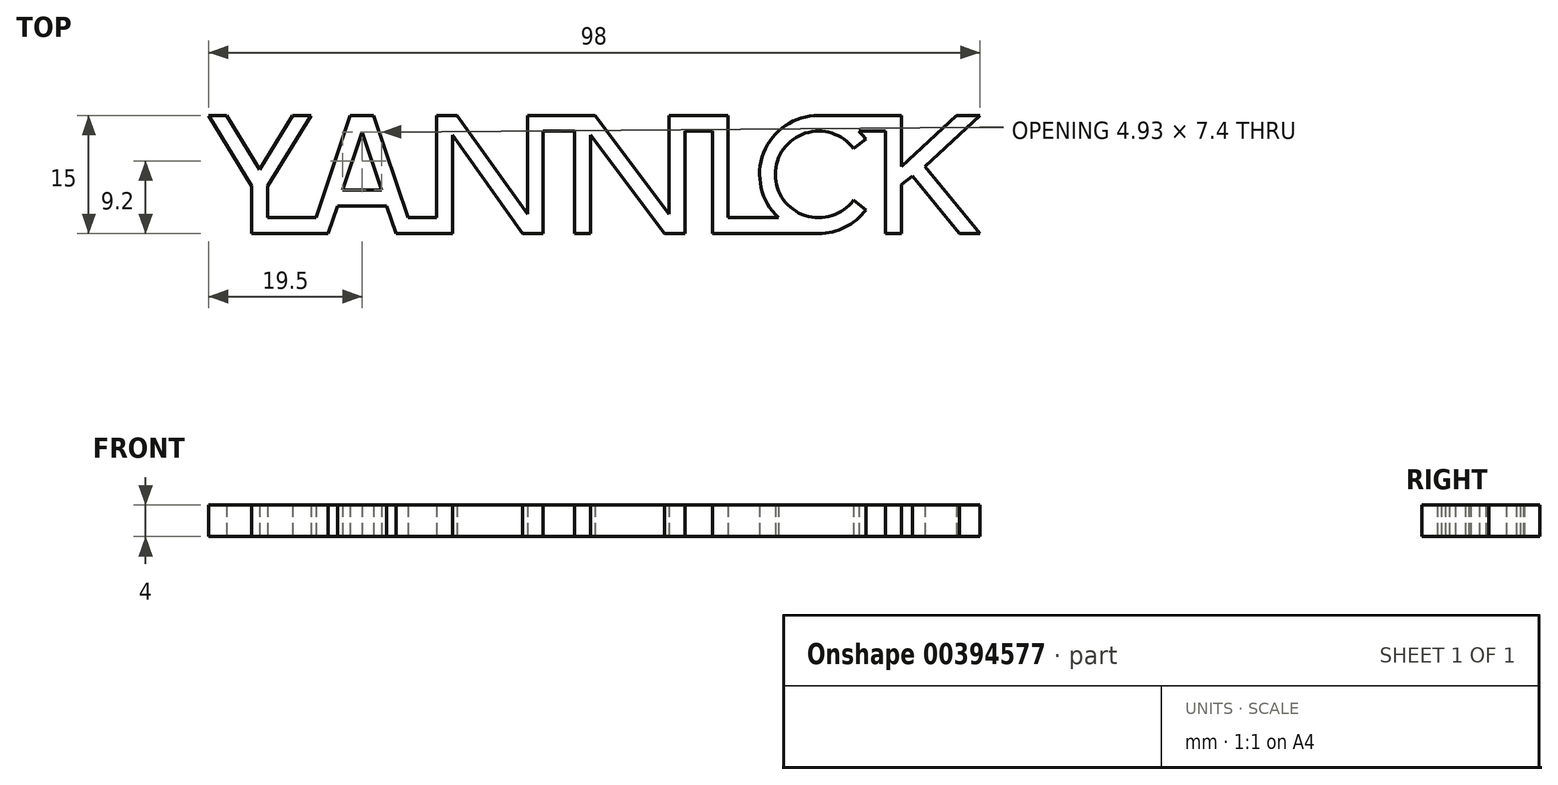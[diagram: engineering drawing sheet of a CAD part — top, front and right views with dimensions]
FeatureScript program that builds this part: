
annotation { "Feature Type Name" : "Feature", "Feature Type Description" : "" }
export const myFeature = defineFeature(function(context is Context, id is Id, definition is map)
    precondition{}
    {
        {
            var Q0;
            Q0=qCreatedBy(makeId("Top.planeOp"),FACE);
            var sketch = newSketch(context, id + "F0", { "sketchPlane" : qUnion([Q0])});
            skPoint(sketch, "E0.middle", {"position": v(0, 0) * mm});
            skLineSegment(sketch, "E1", {"start": v(-38.3, 7.5) * mm, "end": v(-42.5, 0.63) * mm});
            skLineSegment(sketch, "E2", {"start": v(34.5, 4.5) * mm, "end": v(32.93, 3.26) * mm, "construction": true});
            skLineSegment(sketch, "E3", {"start": v(34.5, -4.5) * mm, "end": v(32.93, -3.26) * mm, "construction": true});
            skLineSegment(sketch, "E4", {"start": v(39, 7.5) * mm, "end": v(39, 1) * mm, "construction": true});
            skLineSegment(sketch, "E5", {"start": v(49, 7.5) * mm, "end": v(42, 1) * mm});
            skLineSegment(sketch, "E6", {"start": v(42, 1) * mm, "end": v(49, -7.5) * mm});
            skLineSegment(sketch, "E7", {"start": v(39, -1.27) * mm, "end": v(40.4, -0.2) * mm});
            skLineSegment(sketch, "E8", {"start": v(-42.5, 0.63) * mm, "end": v(-46.7, 7.5) * mm});
            skLineSegment(sketch, "E9", {"start": v(-31.97, -2) * mm, "end": v(-27.03, -2) * mm});
            skLineSegment(sketch, "E10", {"start": v(-32.63, -4) * mm, "end": v(-26.37, -4) * mm});
            skLineSegment(sketch, "E11", {"start": v(-18, 5) * mm, "end": v(-9.1, -7.5) * mm});
            skLineSegment(sketch, "E12", {"start": v(-17.4, 7.5) * mm, "end": v(-8.5, -5) * mm});
            skLineSegment(sketch, "E13", {"start": v(-8.5, 7.5) * mm, "end": v(-8.5, -5) * mm});
            skLineSegment(sketch, "E14", {"start": v(-0.5, -7.5) * mm, "end": v(-0.5, 5) * mm});
            skLineSegment(sketch, "E15", {"start": v(-0.5, 5) * mm, "end": v(8.9, -7.5) * mm});
            skLineSegment(sketch, "E16", {"start": v(9.5, 7.5) * mm, "end": v(9.5, -5) * mm});
            skLineSegment(sketch, "E17", {"start": v(9.5, -5) * mm, "end": v(0.1, 7.5) * mm});
            skArc(sketch, "E18", {"start": v(32.93, 3.26) * mm, "mid": v(23, 0) * mm, "end": v(32.93, -3.26) * mm});
            skLineSegment(sketch, "E19", {"start": v(32.93, 3.26) * mm, "end": v(34.5, 4.5) * mm});
            skLineSegment(sketch, "E20", {"start": v(32.93, -3.26) * mm, "end": v(34.5, -4.5) * mm});
            skLineSegment(sketch, "E21", {"start": v(39, -7.5) * mm, "end": v(39, -1.27) * mm});
            skLineSegment(sketch, "E22", {"start": v(40.4, -0.2) * mm, "end": v(46.4, -7.5) * mm});
            skLineSegment(sketch, "E23", {"start": v(46.4, -7.5) * mm, "end": v(49, -7.5) * mm});
            skLineSegment(sketch, "E24", {"start": v(49, -7.5) * mm, "end": v(42, 1) * mm});
            skLineSegment(sketch, "E25", {"start": v(42, 1) * mm, "end": v(49, 7.5) * mm});
            skLineSegment(sketch, "E26", {"start": v(49, 7.5) * mm, "end": v(46, 7.5) * mm});
            skLineSegment(sketch, "E27", {"start": v(46, 7.5) * mm, "end": v(39, 1) * mm});
            skLineSegment(sketch, "E28", {"start": v(39, 1) * mm, "end": v(39, 7.5) * mm});
            skLineSegment(sketch, "E29", {"start": v(-29.5, 5.4) * mm, "end": v(-27.03, -2) * mm});
            skLineSegment(sketch, "E30", {"start": v(-25.2, -7.5) * mm, "end": v(-26.37, -4) * mm});
            skLineSegment(sketch, "E31", {"start": v(-33.8, -7.5) * mm, "end": v(-32.63, -4) * mm});
            skLineSegment(sketch, "E32", {"start": v(-29.5, 5.4) * mm, "end": v(-31.97, -2) * mm});
            skLineSegment(sketch, "E33", {"start": v(-18, 5) * mm, "end": v(-18, -7.5) * mm});
            skLineSegment(sketch, "E34", {"start": v(-41.5, -5.5) * mm, "end": v(-35.33, -5.5) * mm});
            skLineSegment(sketch, "E35", {"start": v(-23.67, -5.5) * mm, "end": v(-20, -5.5) * mm});
            skLineSegment(sketch, "E36", {"start": v(17, -5.5) * mm, "end": v(23.4, -5.5) * mm});
            skLineSegment(sketch, "E37", {"start": v(37, 5.5) * mm, "end": v(33.6, 5.5) * mm});
            skLineSegment(sketch, "E38", {"start": v(15, 5.5) * mm, "end": v(11.5, 5.5) * mm});
            skLineSegment(sketch, "E39", {"start": v(-2.5, 5.5) * mm, "end": v(-6.5, 5.5) * mm});
            skLineSegment(sketch, "E40", {"start": v(-49, 7.5) * mm, "end": v(-46.7, 7.5) * mm});
            skLineSegment(sketch, "E41", {"start": v(-41.5, -1.5) * mm, "end": v(-41.5, -5.5) * mm});
            skLineSegment(sketch, "E42", {"start": v(-8.5, 7.5) * mm, "end": v(0.1, 7.5) * mm});
            skLineSegment(sketch, "E43", {"start": v(-43.5, -7.5) * mm, "end": v(-33.8, -7.5) * mm});
            skLineSegment(sketch, "E44", {"start": v(-25.2, -7.5) * mm, "end": v(-18, -7.5) * mm});
            skLineSegment(sketch, "E45", {"start": v(-6.5, -7.5) * mm, "end": v(-9.1, -7.5) * mm});
            skLineSegment(sketch, "E46", {"start": v(-2.5, -7.5) * mm, "end": v(-0.5, -7.5) * mm});
            skLineSegment(sketch, "E47", {"start": v(8.9, -7.5) * mm, "end": v(11.5, -7.5) * mm});
            skLineSegment(sketch, "E48", {"start": v(-36, 7.5) * mm, "end": v(-38.3, 7.5) * mm});
            skLineSegment(sketch, "E49", {"start": v(-28, 7.5) * mm, "end": v(-31, 7.5) * mm});
            skLineSegment(sketch, "E50", {"start": v(-20, 7.5) * mm, "end": v(-17.4, 7.5) * mm});
            skLineSegment(sketch, "E51", {"start": v(9.5, 7.5) * mm, "end": v(17, 7.5) * mm});
            skPoint(sketch, "E52", {"position": v(21, 0) * mm});
            skArc(sketch, "E53", {"start": v(34.5, 4.5) * mm, "mid": v(34.07, 5.02) * mm, "end": v(33.6, 5.5) * mm});
            skLineSegment(sketch, "E54", {"start": v(15, -7.5) * mm, "end": v(28.5, -7.5) * mm});
            skArc(sketch, "E55", {"start": v(28.5, -7.5) * mm, "mid": v(31.85, -6.7) * mm, "end": v(34.5, -4.5) * mm});
            skLineSegment(sketch, "E56", {"start": v(39, -7.5) * mm, "end": v(37, -7.5) * mm});
            skLineSegment(sketch, "E57", {"start": v(37, -7.5) * mm, "end": v(37, 5.5) * mm});
            skLineSegment(sketch, "E58", {"start": v(39, 7.5) * mm, "end": v(28.5, 7.5) * mm});
            skLineSegment(sketch, "E59", {"start": v(28.5, 7.5) * mm, "end": v(28.5, 7.5) * mm});
            skArc(sketch, "E60", {"start": v(28.47, 7.5) * mm, "mid": v(21.51, 2.72) * mm, "end": v(23.4, -5.5) * mm});
            skLineSegment(sketch, "E61", {"start": v(33.6, 5.5) * mm, "end": v(33.6, 5.5) * mm});
            skArc(sketch, "E62", {"start": v(28.5, 7.5) * mm, "mid": v(28.48, 7.5) * mm, "end": v(28.47, 7.5) * mm});
            skLineSegment(sketch, "E63", {"start": v(-20, 7.5) * mm, "end": v(-20, -5.5) * mm});
            skLineSegment(sketch, "E64", {"start": v(-28, 7.5) * mm, "end": v(-23.67, -5.5) * mm});
            skLineSegment(sketch, "E65", {"start": v(-31, 7.5) * mm, "end": v(-35.33, -5.5) * mm});
            skLineSegment(sketch, "E66", {"start": v(-36, 7.5) * mm, "end": v(-41.5, -1.5) * mm});
            skLineSegment(sketch, "E67", {"start": v(-42.5, 0.63) * mm, "end": v(-42.5, 0.63) * mm});
            skLineSegment(sketch, "E68", {"start": v(-42.57, 0.51) * mm, "end": v(-42.57, 0.51) * mm});
            skLineSegment(sketch, "E69", {"start": v(-6.5, 5.5) * mm, "end": v(-6.5, -7.5) * mm});
            skLineSegment(sketch, "E70", {"start": v(-2.5, 5.5) * mm, "end": v(-2.5, -7.5) * mm});
            skLineSegment(sketch, "E71", {"start": v(11.5, 5.5) * mm, "end": v(11.5, -7.5) * mm});
            skLineSegment(sketch, "E72", {"start": v(15, 5.5) * mm, "end": v(15, -7.5) * mm});
            skLineSegment(sketch, "E73", {"start": v(17, 7.5) * mm, "end": v(17, -5.5) * mm});
            skPoint(sketch, "E74", {"position": v(-49, -7.5) * mm});
            skLineSegment(sketch, "E75", {"start": v(-47.85, -7.05) * mm, "end": v(-47.85, -7.06) * mm});
            skLineSegment(sketch, "E76", {"start": v(-49, 7.5) * mm, "end": v(-49, 7.5) * mm});
            skLineSegment(sketch, "E77", {"start": v(-46.76, 3.84) * mm, "end": v(-46.76, 3.84) * mm});
            skLineSegment(sketch, "E78", {"start": v(-45.86, 5.5) * mm, "end": v(-45.86, 5.5) * mm});
            skLineSegment(sketch, "E79", {"start": v(-50.47, 3.08) * mm, "end": v(-50.47, 3.08) * mm});
            skLineSegment(sketch, "E80", {"start": v(-43.5, -1.5) * mm, "end": v(-43.5, -7.5) * mm});
            skLineSegment(sketch, "E81", {"start": v(-49, 7.5) * mm, "end": v(-43.5, -1.5) * mm});
            skSolve(sketch);
        }
        {
            var Q0;
            Q0 = qSketchRegion(id + "F0", true);
            extrude(context, id + "F1", {"entities" : qUnion([Q0]), "depth" : 4 * mm});
        }
    });
